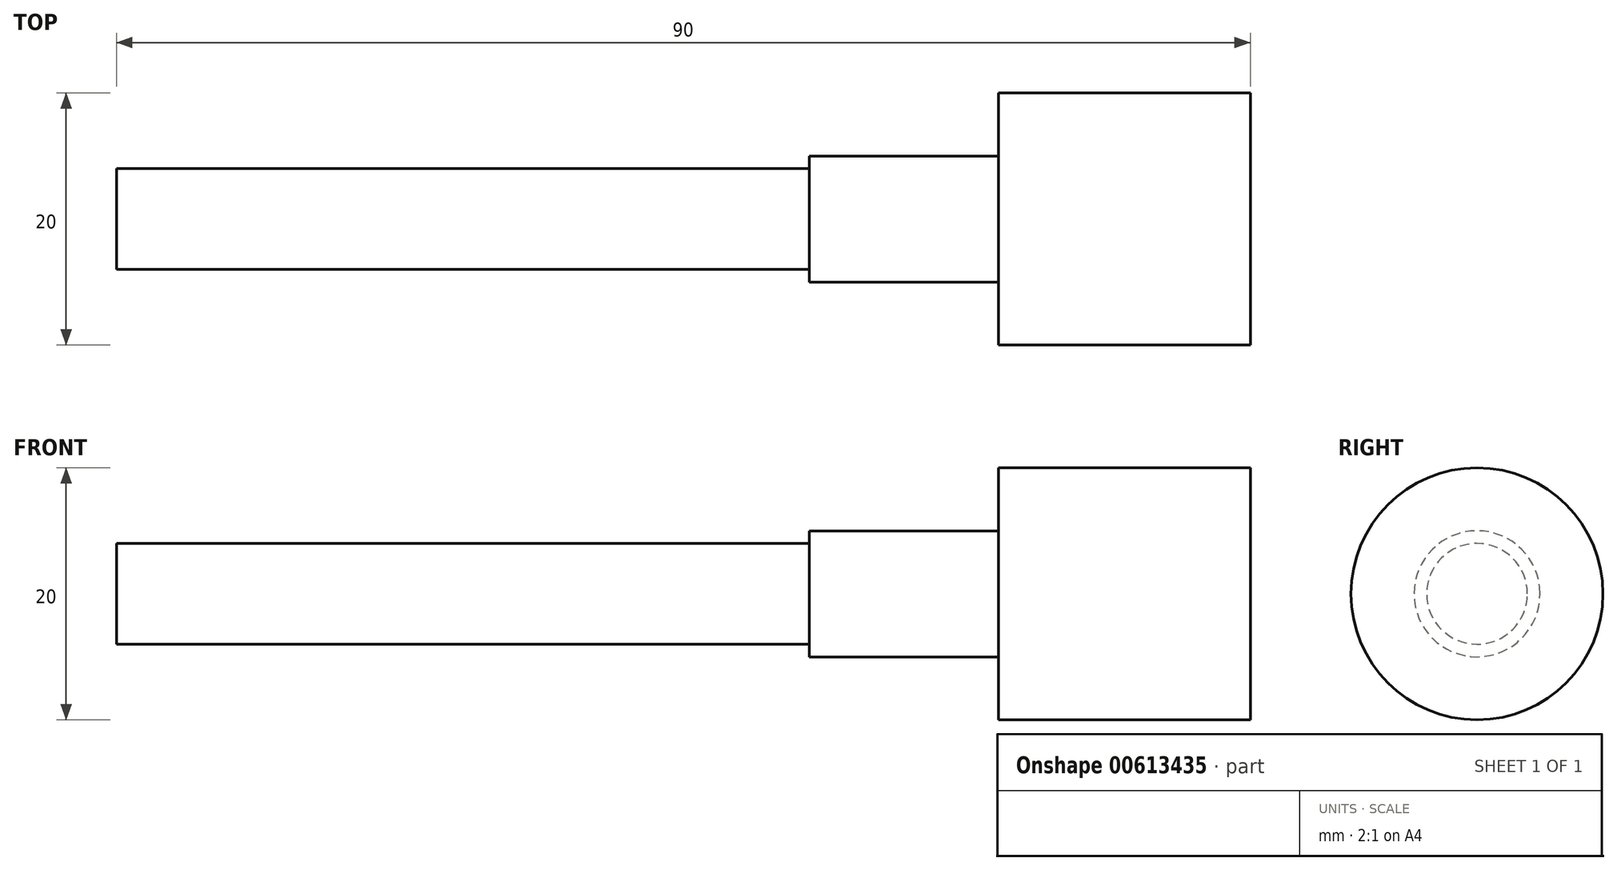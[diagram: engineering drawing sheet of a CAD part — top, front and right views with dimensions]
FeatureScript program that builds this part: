
annotation { "Feature Type Name" : "Feature", "Feature Type Description" : "" }
export const myFeature = defineFeature(function(context is Context, id is Id, definition is map)
    precondition{}
    {
        {
            var Q0;
            Q0=qCreatedBy(makeId("Front.planeOp"),FACE);
            var sketch = newSketch(context, id + "F0", { "sketchPlane" : qUnion([Q0])});
            skLineSegment(sketch, "E0", {"start": v(0, 0) * mm, "end": v(90, 0) * mm});
            skLineSegment(sketch, "E1", {"start": v(0, 18.17) * mm, "end": v(0, -4) * mm});
            skLineSegment(sketch, "E2.0", {"start": v(55, 0) * mm, "end": v(55, -5) * mm});
            skLineSegment(sketch, "E3.0", {"start": v(70, 0) * mm, "end": v(70, -10) * mm});
            skLineSegment(sketch, "E4.0", {"start": v(90, 0) * mm, "end": v(90, -10) * mm});
            skLineSegment(sketch, "E5.0", {"start": v(0, -4) * mm, "end": v(55, -4) * mm});
            skLineSegment(sketch, "E6.0", {"start": v(55, -5) * mm, "end": v(70, -5) * mm});
            skLineSegment(sketch, "E7.0", {"start": v(70, -10) * mm, "end": v(90, -10) * mm});
            skSolve(sketch);
        }
        {
            var Q0;
            {var subQ0=sQuery(id+"F0.wireOp",EDGE,"E6.0");Q0=makeQuery(id+"F0.imprint","IMPRINT",FACE,{"disambiguationData":[TD([[makeQuery(id+"F0.imprint","IMPRINT",EDGE,{"derivedFrom":subQ0}),1.0]])]});}
            var Q1;
            {var subQ5=sQuery(id+"F0.wireOp",EDGE,"E5.0");Q1=makeQuery(id+"F0.imprint","IMPRINT",FACE,{"disambiguationData":[TD([[makeQuery(id+"F0.imprint","IMPRINT",EDGE,{"derivedFrom":subQ5}),1.0]])]});}
            var Q2;
            {var subQ0=sQuery(id+"F0.wireOp",EDGE,"E4.0");Q2=makeQuery(id+"F0.imprint","IMPRINT",FACE,{"disambiguationData":[TD([[makeQuery(id+"F0.imprint","IMPRINT",EDGE,{"derivedFrom":subQ0}),-1.0]])]});}
            var Q3;
            Q3=sQuery(id+"F0.wireOp",EDGE,"E0");
            revolve(context, id + "F1", {"entities" : qUnion([Q0, Q1, Q2]), "axis" : qUnion([Q3]), "revolveType" : RevolveType.FULL});
        }
    });
